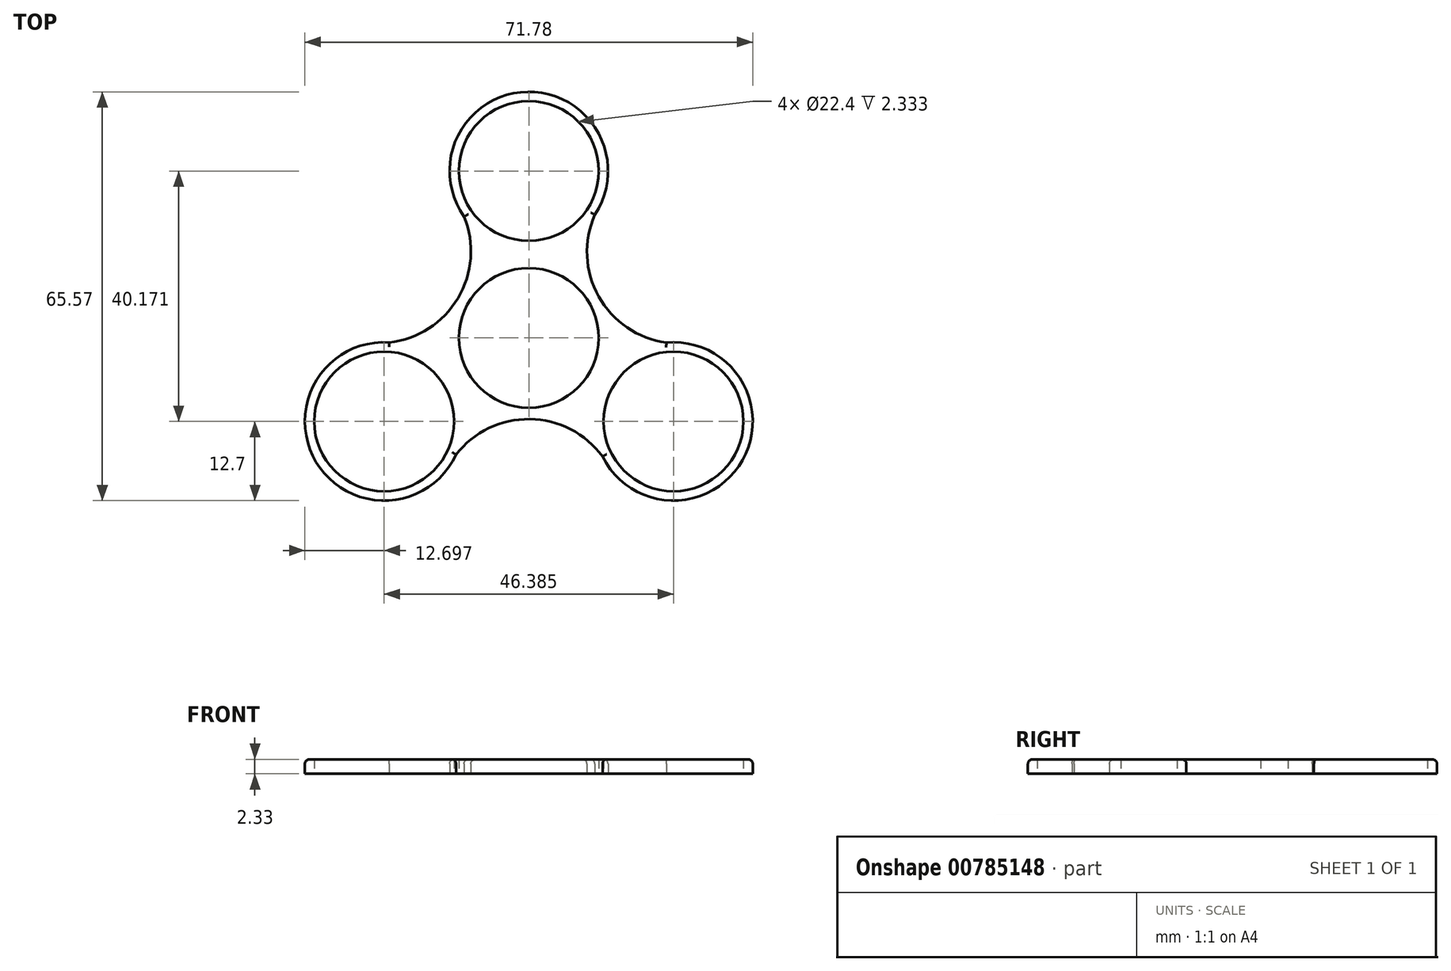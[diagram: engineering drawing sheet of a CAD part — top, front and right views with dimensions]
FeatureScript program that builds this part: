
annotation { "Feature Type Name" : "Feature", "Feature Type Description" : "" }
export const myFeature = defineFeature(function(context is Context, id is Id, definition is map)
    precondition{}
    {
        {
            var Q0;
            Q0=qCreatedBy(makeId("Top.planeOp"),FACE);
            var sketch = newSketch(context, id + "F0", { "sketchPlane" : qUnion([Q0])});
            skCircle(sketch, "E0", {"center": v(0, 0) * mm, "radius": 11.2 * mm});
            skCircle(sketch, "E1", {"center": v(0, 26.78) * mm, "radius": 11.2 * mm});
            skArc(sketch, "E2", {"start": v(10.58, 19.75) * mm, "mid": v(-0.18, 39.48) * mm, "end": v(-10.38, 19.46) * mm});
            skCircle(sketch, "E3.1.0", {"center": v(-23.2, -13.4) * mm, "radius": 11.2 * mm});
            skArc(sketch, "E3.1.1", {"start": v(-22.4, -0.72) * mm, "mid": v(-34.1, -19.9) * mm, "end": v(-11.66, -18.72) * mm});
            skCircle(sketch, "E3.2.0", {"center": v(23.2, -13.4) * mm, "radius": 11.2 * mm});
            skArc(sketch, "E3.2.1", {"start": v(11.82, -19.04) * mm, "mid": v(34.28, -19.59) * mm, "end": v(22.04, -0.74) * mm});
            skArc(sketch, "E4", {"start": v(10.58, 19.75) * mm, "mid": v(11.2, 6.65) * mm, "end": v(22.04, -0.74) * mm});
            skArc(sketch, "E5.1.0", {"start": v(-22.4, -0.72) * mm, "mid": v(-11.36, 6.38) * mm, "end": v(-10.38, 19.46) * mm});
            skArc(sketch, "E5.2.0", {"start": v(11.82, -19.04) * mm, "mid": v(0.16, -13.02) * mm, "end": v(-11.66, -18.72) * mm});
            skLineSegment(sketch, "E6.trimOffspring", {"start": v(11.04, 6.29) * mm, "end": v(11.63, 6.63) * mm});
            skSolve(sketch);
        }
        {
            var Q0;
            Q0=makeQuery(id+"F0.imprint","IMPRINT",FACE,{"disambiguationData":[TD([[makeQuery(id+"F0.imprint","IMPRINT",EDGE,{"derivedFrom":sQuery(id+"F0.wireOp",EDGE,"E0")}),-1.0]])]});
            extrude(context, id + "F1", {"entities" : qUnion([Q0]), "depth" : 2.33 * mm, "offsetDistance" : 25 * mm});
        }
        {
            var Q0;
            Q0=makeQuery(id+"F1.opExtrude","CAP_EDGE",EDGE,{"disambiguationData":[OSD([sQuery(id+"F0.wireOp",EDGE,"E2")])],"isStart":false});
            var Q1;
            Q1=makeQuery(id+"F1.opExtrude","CAP_EDGE",EDGE,{"disambiguationData":[OSD([sQuery(id+"F0.wireOp",EDGE,"E5.1.0")])],"isStart":false});
            var Q2;
            Q2=makeQuery(id+"F1.opExtrude","CAP_EDGE",EDGE,{"disambiguationData":[OSD([sQuery(id+"F0.wireOp",EDGE,"E3.1.1")])],"isStart":false});
            var Q3;
            Q3=makeQuery(id+"F1.opExtrude","CAP_EDGE",EDGE,{"disambiguationData":[OSD([sQuery(id+"F0.wireOp",EDGE,"E5.2.0")])],"isStart":false});
            var Q4;
            Q4=makeQuery(id+"F1.opExtrude","CAP_EDGE",EDGE,{"disambiguationData":[OSD([sQuery(id+"F0.wireOp",EDGE,"E3.2.1")])],"isStart":false});
            var Q5;
            Q5=makeQuery(id+"F1.opExtrude","CAP_EDGE",EDGE,{"disambiguationData":[OSD([sQuery(id+"F0.wireOp",EDGE,"E4")])],"isStart":false});
            fillet(context, id + "F2", {"entities" : qUnion([Q0, Q1, Q2, Q3, Q4, Q5]), "radius" : .75 * mm, "tangentPropagation" : true, "allowEdgeOverflow" : false});
        }
    });
